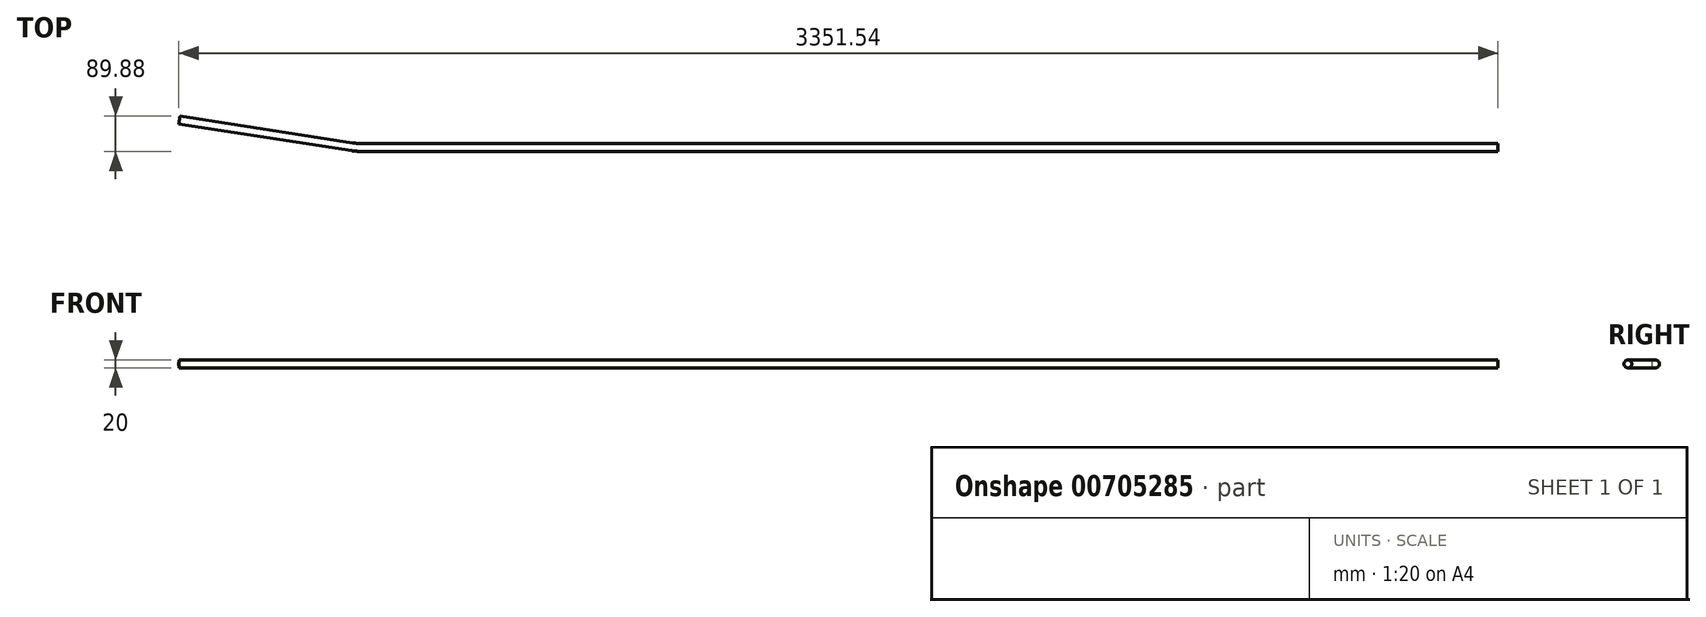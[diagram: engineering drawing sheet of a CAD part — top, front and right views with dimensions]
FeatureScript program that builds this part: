
annotation { "Feature Type Name" : "Feature", "Feature Type Description" : "" }
export const myFeature = defineFeature(function(context is Context, id is Id, definition is map)
    precondition{}
    {
        {
            var Q0;
            Q0=qCreatedBy(makeId("Top.planeOp"),FACE);
            var sketch = newSketch(context, id + "F0", { "sketchPlane" : qUnion([Q0])});
            skLineSegment(sketch, "E0", {"start": v(0, -150) * mm, "end": v(438.54, -218.22) * mm});
            skLineSegment(sketch, "E1", {"start": v(461.6, -220) * mm, "end": v(3350, -220) * mm});
            skPoint(sketch, "E2.visualSharp", {"position": v(450, -220) * mm});
            skArc(sketch, "E2.filletArc", {"start": v(438.54, -218.22) * mm, "mid": v(450.03, -219.55) * mm, "end": v(461.6, -220) * mm});
            skSolve(sketch);
        }
        {
            var Q0;
            Q0=sQuery(id+"F0.wireOp",VERTEX,"E1.end");
            var Q1;
            Q1=sQuery(id+"F0.wireOp",EDGE,"E1");
            cPlane(context, id + "F1", {"entities" : qUnion([Q0, Q1]), "cplaneType" : CPlaneType.LINE_POINT, "offset" : 25 * mm, "width" : 150 * mm, "height" : 150 * mm});
        }
        {
            var Q0;
            Q0=qCreatedBy(id+"F1.planeOp",FACE);
            var sketch = newSketch(context, id + "F2", { "sketchPlane" : qUnion([Q0])});
            skCircle(sketch, "E3", {"center": v(-220, 0) * mm, "radius": 10 * mm});
            skSolve(sketch);
        }
        {
            var Q0;
            Q0=makeQuery(id+"F2.imprint","IMPRINT",FACE,{"disambiguationData":[TD([[makeQuery(id+"F2.imprint","IMPRINT",EDGE,{"derivedFrom":sQuery(id+"F2.wireOp",EDGE,"E3")}),1.0]])]});
            var Q1;
            Q1=sQuery(id+"F0.wireOp",EDGE,"E1");
            var Q2;
            Q2=sQuery(id+"F0.wireOp",EDGE,"E2.filletArc");
            var Q3;
            Q3=sQuery(id+"F0.wireOp",EDGE,"E0");
            sweep(context, id + "F3", {"profiles" : qUnion([Q0]), "path" : qUnion([Q1, Q2, Q3])});
        }
    });
